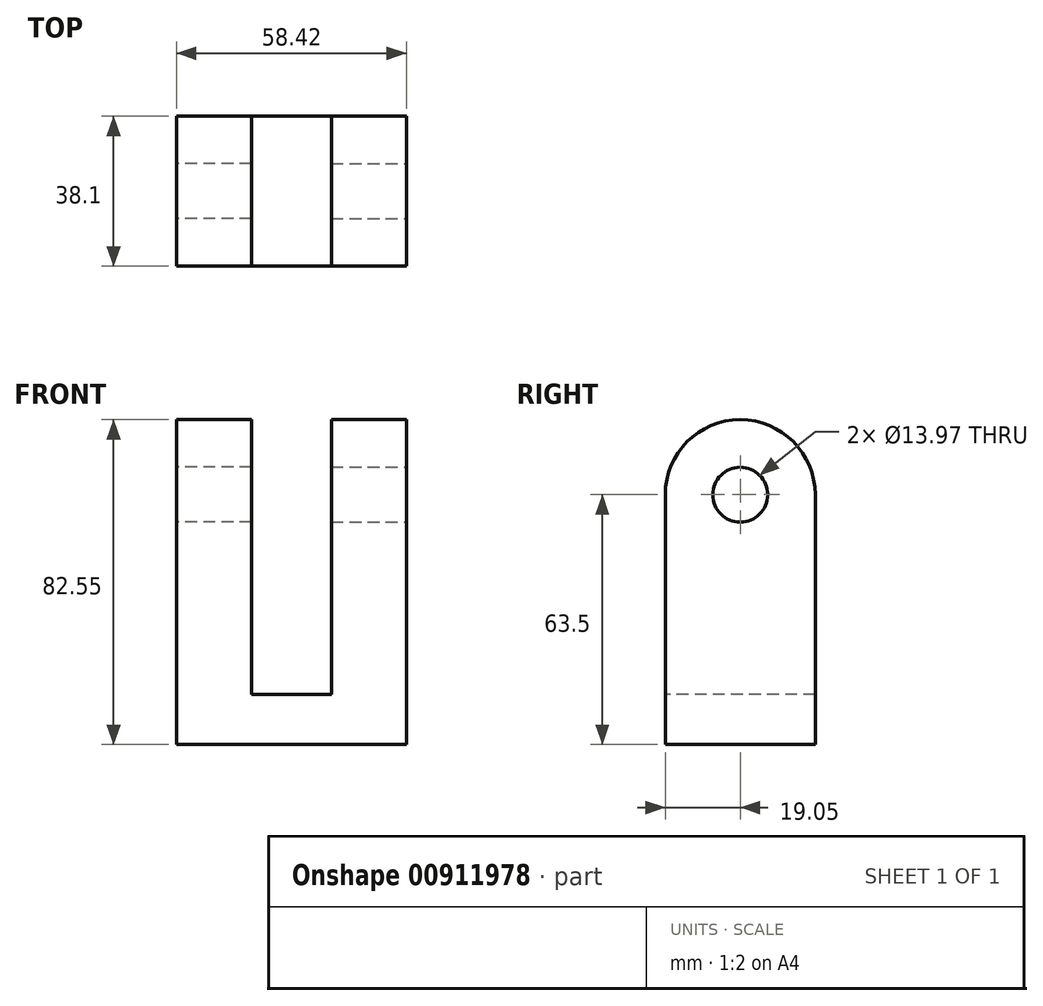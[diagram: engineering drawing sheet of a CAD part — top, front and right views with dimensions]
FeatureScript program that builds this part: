
annotation { "Feature Type Name" : "Feature", "Feature Type Description" : "" }
export const myFeature = defineFeature(function(context is Context, id is Id, definition is map)
    precondition{}
    {
        {
            var Q0;
            Q0=qCreatedBy(makeId("Top.planeOp"),FACE);
            var sketch = newSketch(context, id + "F0", { "sketchPlane" : qUnion([Q0])});
            skLineSegment(sketch, "E0.bottom", {"start": v(-29.2, 19.05) * mm, "end": v(29.21, 19.05) * mm});
            skLineSegment(sketch, "E0.top", {"start": v(-29.21, -19.05) * mm, "end": v(29.2, -19.05) * mm});
            skLineSegment(sketch, "E0.left", {"start": v(-29.2, 19.05) * mm, "end": v(-29.21, -19.05) * mm});
            skLineSegment(sketch, "E0.right", {"start": v(29.21, 19.05) * mm, "end": v(29.2, -19.05) * mm});
            skPoint(sketch, "E0.middle", {"position": v(0, 0) * mm});
            skSolve(sketch);
        }
        {
            var Q0;
            Q0=makeQuery(id+"F0.imprint","IMPRINT",FACE,{"disambiguationData":[TD([[makeQuery(id+"F0.imprint","IMPRINT",EDGE,{"derivedFrom":sQuery(id+"F0.wireOp",EDGE,"E0.bottom")}),-1.0]])]});
            extrude(context, id + "F1", {"entities" : qUnion([Q0]), "oppositeDirection" : true, "depth" : 12.7 * mm, "offsetDistance" : 25.4 * mm});
        }
        {
            var Q0;
            Q0=makeQuery(id+"F1.opExtrude","SWEPT_FACE",FACE,{"disambiguationData":[OSD([sQuery(id+"F0.wireOp",EDGE,"E0.right")])]});
            var sketch = newSketch(context, id + "F2", { "sketchPlane" : qUnion([Q0])});
            skCircle(sketch, "E1", {"center": v(0, 50.8) * mm, "radius": 6.99 * mm});
            skLineSegment(sketch, "E2.bottom", {"start": v(19.05, 0) * mm, "end": v(-19.05, 0) * mm});
            skLineSegment(sketch, "E2.left", {"start": v(19.05, 0) * mm, "end": v(19.05, 50.8) * mm});
            skLineSegment(sketch, "E2.right", {"start": v(-19.05, 0) * mm, "end": v(-19.05, 50.8) * mm});
            skArc(sketch, "E3", {"start": v(19.05, 50.8) * mm, "mid": v(0, 69.85) * mm, "end": v(-19.05, 50.8) * mm});
            skSolve(sketch);
        }
        {
            var Q0;
            Q0=makeQuery(id+"F2.imprint","IMPRINT",FACE,{"disambiguationData":[TD([[makeQuery(id+"F2.imprint","IMPRINT",EDGE,{"derivedFrom":sQuery(id+"F2.wireOp",EDGE,"E1")}),-1.0]])]});
            extrude(context, id + "F3", {"entities" : qUnion([Q0]), "operationType" : NewBodyOperationType.ADD, "oppositeDirection" : true, "depth" : 19.05 * mm, "offsetDistance" : 25.4 * mm});
        }
        {
            var Q0;
            Q0=makeQuery(id+"F1.opExtrude","SWEPT_BODY",BODY,{"disambiguationData":[OSD([sQuery(id+"F0.wireOp",EDGE,"E0.bottom"),sQuery(id+"F0.wireOp",EDGE,"E0.top"),sQuery(id+"F0.wireOp",EDGE,"E0.left"),sQuery(id+"F0.wireOp",EDGE,"E0.right")])]});
            var Q1;
            Q1=qCreatedBy(makeId("Right.planeOp"),FACE);
            mirror(context, id + "F4", {"operationType" : NewBodyOperationType.ADD, "entities" : qUnion([Q0]), "mirrorPlane" : qUnion([Q1])});
        }
    });
